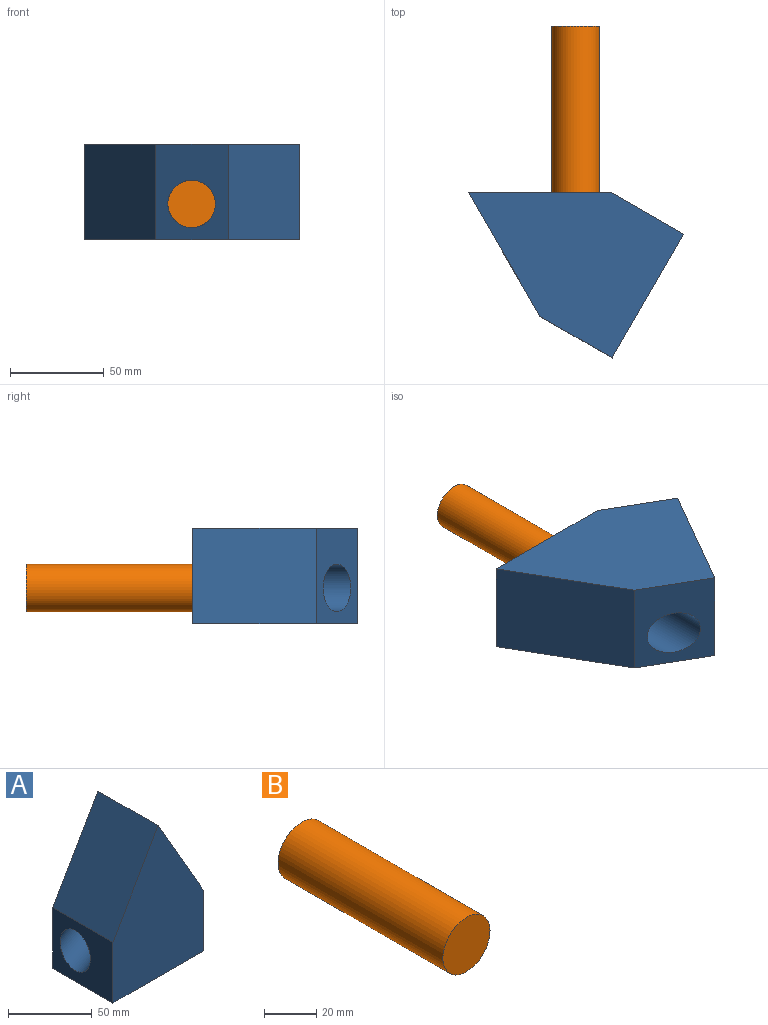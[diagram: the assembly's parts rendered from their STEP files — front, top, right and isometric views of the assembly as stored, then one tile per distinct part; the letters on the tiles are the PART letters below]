
ASSEMBLY  parts=2 mates=1
PART A: 8 faces, bbox 92x53.9x113.5 mm
  f0: plane 50.8x44.45mm, normal (1,0,0), area 2258.1mm2, adj f1,f4,f5,f6
  f1: plane 65.99x50.8mm, normal (0.87,0,0.5), area 3364.3mm2, adj f0,f2,f5,f6,f7
  f2: plane 65.99x50.8mm, normal (-0.87,0,0.5), area 3871mm2, adj f1,f3,f5,f6
  f3: plane 53.88x47.53mm, normal (-1,0,0), area 1673mm2, adj f2,f4,f5,f6,f7
  f4: plane 76.2x50.8mm, normal (0,0,-1), area 3871mm2, adj f0,f3,f5,f6
  f5: plane 110.44x76.2mm, normal (0,-1,0), area 5901.4mm2, adj f0,f1,f2,f3,f4
  f6: plane 110.44x76.2mm, normal (0,1,0), area 5901.4mm2, adj f0,f1,f2,f3,f4
  f7: cylinder r=12.7mm len=85.73mm, axis (0.87,0,0.5), area 6143.5mm2, adj f1,f3
PART B: 3 faces, bbox 25.4x88.9x25.4 mm
  f0: cylinder r=12.7mm len=88.9mm, axis (0,1,0), area 7093.9mm2, adj f1,f2
  f1: plane 25.4x25.4mm, normal (0,-1,0), area 506.7mm2, adj f0
  f2: plane 25.4x25.4mm, normal (0,1,0), area 506.7mm2, adj f0
PLACE A rot(axis=(-0.77,-0.45,0.45),104.5deg) t=(0.47,-141.89,-16.46)mm fixed
PLACE B t=(-18.97,35.22,2.59)mm
MATE revolute A.f7 <-> B.f0  axis (0,1,0) through (-18.97,-53.68,2.59)mm
